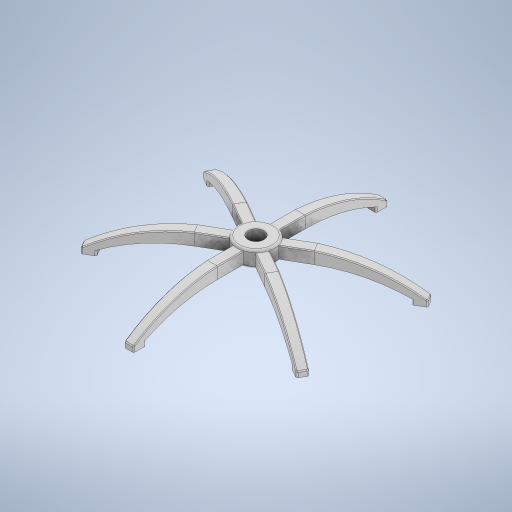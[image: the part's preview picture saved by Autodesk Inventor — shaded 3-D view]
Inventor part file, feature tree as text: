
AUTODESK INVENTOR PART (.ipt)
format: ipt  version: 2023 (Build 270158030, 158C)  size: 633,856 bytes
history: native  units: in
note: dims shown in document units (in); Inventor stores cm internally (conversion verified against a paired STEP export)
features: extrude x4, sketch x4, fillet x2, chamfer x1, pattern_circular x1
ambient origin geometry x8: Origin, YZ Plane, XZ Plane, XY Plane, X Axis, Y Axis, Z Axis, Center Point
bodies: Solid1 (feature_tree)
feature tree (12):
  extrude  "Extrusion1"  Depth=1.5in
  fillet  "Fillet1"  Radius=1.5in
  extrude  "Extrusion2"  Depth=0.25in
  extrude  "Extrusion7"  Depth=2.5in
  extrude  "Extrusion8"  Depth=1.0in TaperAngle=0.0deg
  fillet  "Fillet2"  Radius=7.0in
  chamfer  "Chamfer1"  Distance=1.5883in
  pattern_circular  "Circular Pattern3"  [2 undecoded]
  sketch  "Sketch1"  dims[d0=3.5in d1=1.5in d2=1.5in d3=0.0in]
  sketch  "Sketch2"  dims[d4=0.2in d5=0.25in]
  sketch  "Sketch7"  dims[d7=0.25in d8=2.5in]
  sketch  "Sketch8"  dims[d12=2.6195in d16=1.0in d17=0.0in d47=7.0in d48=1.5883in d49=1.1in d50=15.4254in d51=15.425in d52=0.5in d68=9.0674in d69=0.0034in d70=0.0034in d71=1.0in d72=0.0in d73=1.1in d74=0.7063in d75=0.5in d76=0.5in d77=0.0in d81=0.125in d82=0.075in d83=0.125in d84=45.0deg d85=2.3622in d86=360.0deg]
note: 2 required parameter values undecoded (feature->parameter linkage not recoverable at this tier; creation-order binding heuristic only, values carry confidence <= 0.55)
